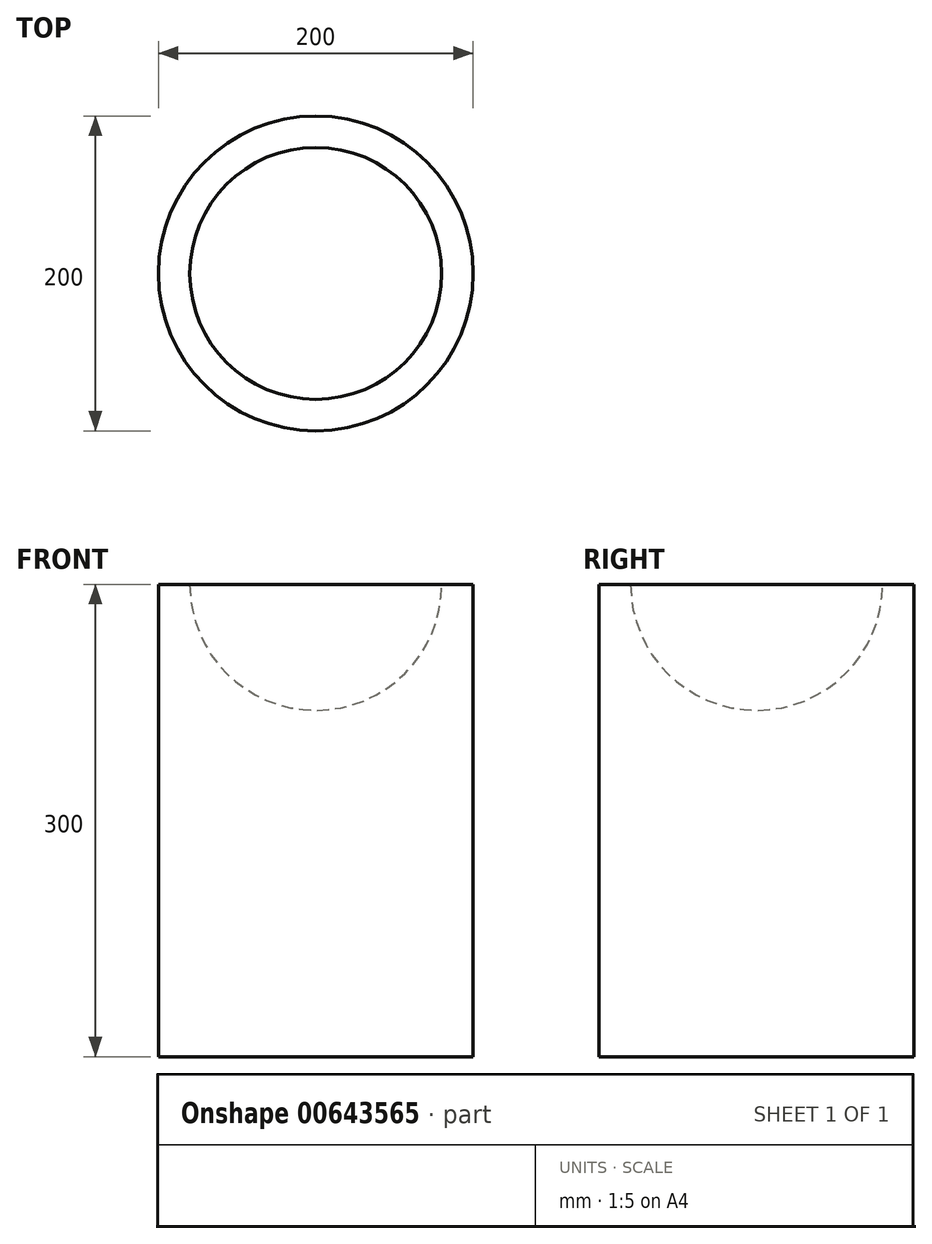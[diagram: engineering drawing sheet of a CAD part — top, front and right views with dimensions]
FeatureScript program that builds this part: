
annotation { "Feature Type Name" : "Feature", "Feature Type Description" : "" }
export const myFeature = defineFeature(function(context is Context, id is Id, definition is map)
    precondition{}
    {
        {
            var Q0;
            Q0=qCreatedBy(makeId("Top.planeOp"),FACE);
            var sketch = newSketch(context, id + "F0", { "sketchPlane" : qUnion([Q0])});
            skCircle(sketch, "E0", {"center": v(0, 0) * mm, "radius": 100 * mm});
            skSolve(sketch);
        }
        {
            var Q0;
            Q0=makeQuery(id+"F0.imprint","IMPRINT",FACE,{"disambiguationData":[TD([[makeQuery(id+"F0.imprint","IMPRINT",EDGE,{"derivedFrom":sQuery(id+"F0.wireOp",EDGE,"E0")}),1.0]])]});
            extrude(context, id + "F1", {"entities" : qUnion([Q0]), "depth" : 300 * mm, "offsetDistance" : 25 * mm});
        }
        {
            var Q0;
            Q0=makeQuery(id+"F1.opExtrude","CAP_FACE",FACE,{"disambiguationData":[OSD([sQuery(id+"F0.wireOp",EDGE,"E0")])],"isStart":false});
            var sketch = newSketch(context, id + "F2", { "sketchPlane" : qUnion([Q0])});
            skSolve(sketch);
        }
        {
            var Q0;
            Q0=makeQuery(id+"F2.imprint","IMPRINT",FACE,{"disambiguationData":[TD([[makeQuery(id+"F2.imprint","IMPRINT",EDGE,{"derivedFrom":makeQuery(id+"F1.opExtrude","CAP_EDGE",EDGE,{"disambiguationData":[OSD([sQuery(id+"F0.wireOp",EDGE,"E0")])],"isStart":false})}),1.0]])]});
            var sketch = newSketch(context, id + "F3", { "sketchPlane" : qUnion([Q0])});
            skCircle(sketch, "E1", {"center": v(0, 0) * mm, "radius": 80 * mm});
            skLineSegment(sketch, "E2", {"start": v(0, -80) * mm, "end": v(0, 80) * mm});
            skSolve(sketch);
        }
        {
            var Q0;
            {var subQ0=sQuery(id+"F3.wireOp",EDGE,"E2");Q0=makeQuery(id+"F3.imprint","IMPRINT",FACE,{"disambiguationData":[TD([[makeQuery(id+"F3.imprint","IMPRINT",EDGE,{"derivedFrom":subQ0}),-1.0]])]});}
            var Q1;
            Q1=sQuery(id+"F3.wireOp",EDGE,"E2");
            revolve(context, id + "F4", {"operationType" : NewBodyOperationType.REMOVE, "entities" : qUnion([Q0]), "axis" : qUnion([Q1]), "revolveType" : RevolveType.FULL, "oppositeDirection" : true});
        }
    });
